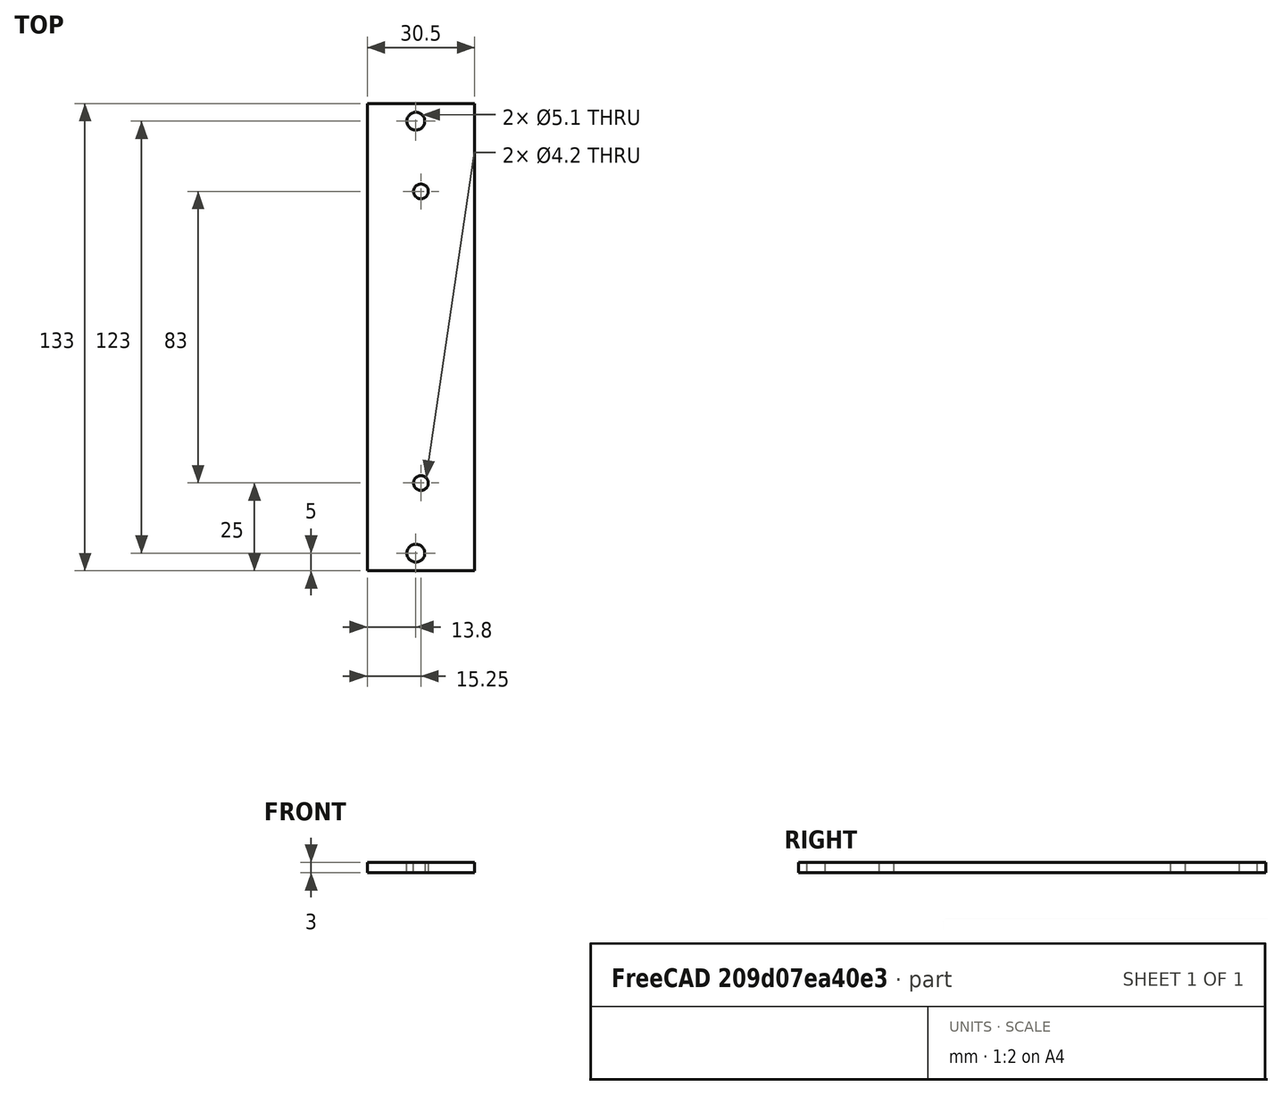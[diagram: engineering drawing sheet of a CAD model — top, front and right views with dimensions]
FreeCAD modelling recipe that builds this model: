
FCSTD DOCUMENT  (FreeCAD 0.17R13541 (Git))
Label: Sidepanel_3HE
License: All rights reserved
LicenseURL: http://en.wikipedia.org/wiki/All_rights_reserved
objects: TechDraw::DrawViewDimension×14, Sketcher::SketchObject×2, TechDraw::DrawProjGroupItem×2, PartDesign::Pad×1, PartDesign::Pocket×1, PartDesign::Body×1, TechDraw::DrawSVGTemplate×1, TechDraw::DrawProjGroup×1, TechDraw::DrawPage×1
note: 7 computed .brp shape members not serialized (recipe doc carries the construction recipe); baked Part::Feature solids carry a one-line shape summary decoded from their .brp

FEATURE [Sketcher::SketchObject] Sketch
  MapMode = 5
  Support = -> [XY_Plane]
  sketch-geometry (4):
    g0: LineSegment StartX=-30.5 StartY=133 StartZ=0 EndX=0 EndY=133 EndZ=0
    g1: LineSegment StartX=0 StartY=133 StartZ=0 EndX=0 EndY=0 EndZ=0
    g2: LineSegment StartX=0 StartY=0 StartZ=0 EndX=-30.5 EndY=0 EndZ=0
    g3: LineSegment StartX=-30.5 StartY=0 StartZ=0 EndX=-30.5 EndY=133 EndZ=0
  constraints (11):
    c: Coincident(g0,g1)
    c: Coincident(g1,g2)
    c: Coincident(g2,g3)
    c: Coincident(g3,g0)
    c: Horizontal(g0)
    c: Horizontal(g2)
    c: Vertical(g1)
    c: Vertical(g3)
    c: DistanceX(g0,g0) = 30.5
    c: DistanceY(g1,g1) = 133
    c: Coincident(g-1,g1)
FEATURE [PartDesign::Pad] Pad
  Length = 3
  Length2 = 100
  Profile = -> Sketch
  Type = 0
FEATURE [Sketcher::SketchObject] Sketch001
  ExternalGeometry = -> [Pad]
  MapMode = 5
  Placement = pos=(0,0,3) rot=(0,0,1;0rad)
  Support = -> [Pad]
  sketch-geometry (4):
    g0: Circle CenterX=-16.7 CenterY=5 CenterZ=0 NormalX=0 NormalY=0 NormalZ=1 AngleXU=0 Radius=2.55
    g1: Circle CenterX=-16.7 CenterY=128 CenterZ=0 NormalX=0 NormalY=0 NormalZ=1 AngleXU=0 Radius=2.55
    g2: Circle CenterX=-15.25 CenterY=25 CenterZ=0 NormalX=0 NormalY=0 NormalZ=1 AngleXU=0 Radius=2.1
    g3: Circle CenterX=-15.25 CenterY=108 CenterZ=0 NormalX=0 NormalY=0 NormalZ=1 AngleXU=0 Radius=2.1
  constraints (12):
    c: DistanceY(g-1,g0) = 5
    c: DistanceX(g-6,g0) = 13.8
    c: Radius(g0) = 2.55
    c: Radius(g1) = 2.55
    c: DistanceY(g1,g-4) = 5
    c: DistanceX(g-6,g1) = 13.8
    c: DistanceX(g3,g-4) = 15.25
    c: DistanceX(g2,g-1) = 15.25
    c: DistanceY(g3,g-4) = 25
    c: DistanceY(g-1,g2) = 25
    c: Radius(g3) = 2.1
    c: Radius(g2) = 2.1
FEATURE [PartDesign::Pocket] Pocket
  BaseFeature = -> Pad
  Length = 5
  Length2 = 100
  Profile = -> Sketch001
  Type = 1
FEATURE [PartDesign::Body] Body
  Group = -> [Sketch,Pad,Sketch001,Pocket]
  Origin = -> Origin
  Tip = -> Pocket
FEATURE [TechDraw::DrawSVGTemplate] Template
  EditableTexts = Designed_by_Name=Oliver Walczak; Drawing_number=1; FC-Date=27.12.2018; FC-SC=2; FC-SH=1; FC-Title=Sidepanel 3HE; Weight=-
  Height = 210
  Orientation = 1
  Width = 297
FEATURE [TechDraw::DrawProjGroupItem] ProjItem  label="Front"
  CoarseView = false
  Direction = (0,0,-1)
  Focus = 100
  HardHidden = false
  IsoCount = 0
  IsoHidden = false
  IsoVisible = false
  LockPosition = false
  Perspective = false
  Rotation = 0
  RotationVector = (1,0,0)
  ScaleType = 0
  SeamHidden = false
  SeamVisible = false
  SmoothHidden = false
  SmoothVisible = false
  Source = -> [Body]
  Type = 0
  X = -72.297
  Y = -35.1824
FEATURE [TechDraw::DrawProjGroupItem] ProjItem002  label="Persp"
  CoarseView = false
  Direction = (-1,-1,-1)
  Focus = 100
  HardHidden = false
  IsoCount = 0
  IsoHidden = false
  IsoVisible = false
  LockPosition = false
  Perspective = false
  Rotation = 0
  RotationVector = (1,0,-1)
  ScaleType = 0
  SeamHidden = false
  SeamVisible = false
  SmoothHidden = false
  SmoothVisible = false
  Source = -> [Body]
  Type = 6
  X = 136.181
  Y = 12.21
FEATURE [TechDraw::DrawProjGroup] ProjGroup
  Anchor = -> ProjItem
  AutoDistribute = false
  CubeDirs = (6) [(0,1,-6.12323e-17),(0,-6.12323e-17,-1),(-1,0,0),(0,6.12323e-17,1),(1,0,0),(0,-1,6.12323e-17)]
  CubeRotations = (6) [(1,0,0),(1,0,0),(0,-6.12323e-17,-1),(-1,0,0),(0,6.12323e-17,1),(1,0,0)]
  LockPosition = false
  ProjectionType = 0
  Rotation = 0
  ScaleType = 0
  Source = -> [Body]
  Views = -> [ProjItem,ProjItem002]
  X = 83.8574
  Y = 116.787
  spacingX = 15
  spacingY = 15
FEATURE [TechDraw::DrawViewDimension] Dimension
  FormatSpec = %.2f
  LockPosition = false
  MeasureType = 1
  References2D = -> [ProjItem]
  Rotation = 0
  ScaleType = 0
  Type = 2
  X = -32.1894
  Y = -78.2536
FEATURE [TechDraw::DrawViewDimension] Dimension001
  FormatSpec = %.2f
  LockPosition = false
  MeasureType = 1
  References2D = -> [ProjItem]
  Rotation = 0
  ScaleType = 0
  Type = 2
  X = -39.1268
  Y = -53.2791
FEATURE [TechDraw::DrawViewDimension] Dimension002
  FormatSpec = %.2f
  LockPosition = false
  MeasureType = 1
  References2D = -> [ProjItem]
  Rotation = 0
  ScaleType = 0
  Type = 2
  X = 20.8121
  Y = 0
FEATURE [TechDraw::DrawViewDimension] Dimension003
  FormatSpec = %.2f
  LockPosition = false
  MeasureType = 1
  References2D = -> [ProjItem]
  Rotation = 0
  ScaleType = 0
  Type = 1
  X = -0.832485
  Y = -87.411
FEATURE [TechDraw::DrawViewDimension] Dimension004
  FormatSpec = %.2f
  LockPosition = false
  MeasureType = 1
  References2D = -> [ProjItem]
  Rotation = 0
  ScaleType = 0
  Type = 2
  X = -26.0845
  Y = 51.8916
FEATURE [TechDraw::DrawViewDimension] Dimension005
  FormatSpec = %.2f
  LockPosition = false
  MeasureType = 1
  References2D = -> [ProjItem]
  Rotation = 0
  ScaleType = 0
  Type = 2
  X = -37.4618
  Y = 53.2791
FEATURE [TechDraw::DrawViewDimension] Dimension006
  FormatSpec = %.2f
  LockPosition = false
  MeasureType = 1
  References2D = -> [ProjItem]
  Rotation = 0
  ScaleType = 0
  Type = 5
  X = 43.9787
  Y = 47.8488
FEATURE [TechDraw::DrawViewDimension] Dimension007
  FormatSpec = %.2f
  LockPosition = false
  MeasureType = 1
  References2D = -> [ProjItem]
  Rotation = 0
  ScaleType = 0
  Type = 5
  X = 42.3955
  Y = 29.2019
FEATURE [TechDraw::DrawViewDimension] Dimension008
  FormatSpec = %.2f
  LockPosition = false
  MeasureType = 1
  References2D = -> [ProjItem]
  Rotation = 0
  ScaleType = 0
  Type = 5
  X = 46.2043
  Y = -35.2364
FEATURE [TechDraw::DrawViewDimension] Dimension009
  FormatSpec = %.2f
  LockPosition = false
  MeasureType = 1
  References2D = -> [ProjItem]
  Rotation = 0
  ScaleType = 0
  Type = 5
  X = 38.9169
  Y = -19.7357
FEATURE [TechDraw::DrawViewDimension] Dimension010
  FormatSpec = %.2f
  LockPosition = false
  MeasureType = 1
  References2D = -> [ProjItem]
  Rotation = 0
  ScaleType = 0
  Type = 1
  X = -3.88493
  Y = 73.8137
FEATURE [TechDraw::DrawViewDimension] Dimension011
  FormatSpec = %.2f
  LockPosition = false
  MeasureType = 1
  References2D = -> [ProjItem]
  Rotation = 0
  ScaleType = 0
  Type = 1
  X = -27.472
  Y = 33.0219
FEATURE [TechDraw::DrawViewDimension] Dimension012
  FormatSpec = %.2f
  LockPosition = false
  MeasureType = 1
  References2D = -> [ProjItem]
  Rotation = 0
  ScaleType = 0
  Type = 1
  X = -3.32994
  Y = -78.8086
FEATURE [TechDraw::DrawViewDimension] Dimension013
  FormatSpec = %.2f
  LockPosition = false
  MeasureType = 1
  References2D = -> [ProjItem]
  Rotation = 0
  ScaleType = 0
  Type = 1
  X = -27.472
  Y = -28.027
FEATURE [TechDraw::DrawPage] Page  label="Sidepanel 3HE"
  KeepUpdated = true
  ProjectionType = 0
  Template = -> Template
  Views = -> [ProjGroup,Dimension,Dimension001,Dimension002,Dimension003,Dimension004,Dimension005,Dimension006,Dimension007,Dimension008,Dimension009,Dimension010,Dimension011,Dimension012,Dimension013]
